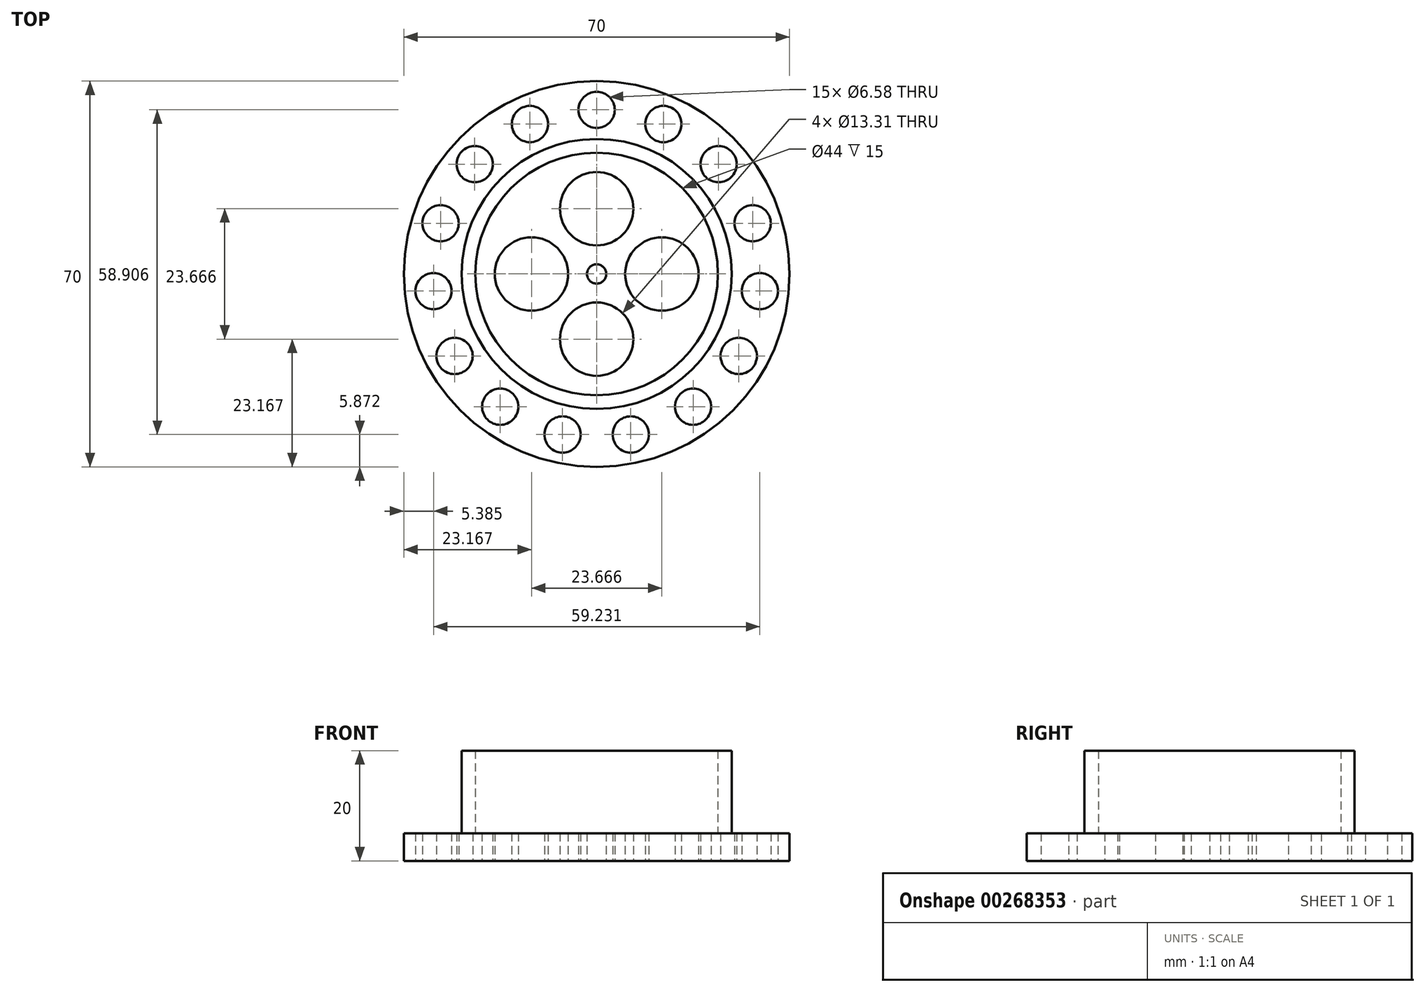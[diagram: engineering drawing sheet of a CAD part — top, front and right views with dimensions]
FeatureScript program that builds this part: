
annotation { "Feature Type Name" : "Feature", "Feature Type Description" : "" }
export const myFeature = defineFeature(function(context is Context, id is Id, definition is map)
    precondition{}
    {
        {
            var Q0;
            Q0=qCreatedBy(makeId("Top.planeOp"),FACE);
            var sketch = newSketch(context, id + "F0", { "sketchPlane" : qUnion([Q0])});
            skCircle(sketch, "E0", {"center": v(0, 0) * mm, "radius": 35 * mm});
            skCircle(sketch, "E1", {"center": v(0, 0) * mm, "radius": 22 * mm});
            skCircle(sketch, "E2", {"center": v(0, 0) * mm, "radius": 24.5 * mm});
            skCircle(sketch, "E3", {"center": v(0, 0) * mm, "radius": 1.75 * mm});
            skCircle(sketch, "E4", {"center": v(0, 11.83) * mm, "radius": 6.66 * mm});
            skCircle(sketch, "E5", {"center": v(0, 29.78) * mm, "radius": 3.29 * mm});
            skCircle(sketch, "E6.1.0", {"center": v(-12.11, 27.2) * mm, "radius": 3.29 * mm});
            skCircle(sketch, "E6.2.0", {"center": v(-22.13, 19.93) * mm, "radius": 3.29 * mm});
            skCircle(sketch, "E6.3.0", {"center": v(-28.32, 9.2) * mm, "radius": 3.29 * mm});
            skCircle(sketch, "E6.4.0", {"center": v(-29.62, -3.11) * mm, "radius": 3.29 * mm});
            skCircle(sketch, "E6.5.0", {"center": v(-25.79, -14.89) * mm, "radius": 3.29 * mm});
            skCircle(sketch, "E6.6.0", {"center": v(-17.5, -24.1) * mm, "radius": 3.29 * mm});
            skCircle(sketch, "E6.7.0", {"center": v(-6.2, -29.13) * mm, "radius": 3.29 * mm});
            skCircle(sketch, "E6.8.0", {"center": v(6.2, -29.13) * mm, "radius": 3.29 * mm});
            skCircle(sketch, "E6.9.0", {"center": v(17.5, -24.1) * mm, "radius": 3.29 * mm});
            skCircle(sketch, "E6.10.0", {"center": v(25.79, -14.89) * mm, "radius": 3.29 * mm});
            skCircle(sketch, "E6.11.0", {"center": v(29.62, -3.11) * mm, "radius": 3.29 * mm});
            skCircle(sketch, "E6.12.0", {"center": v(28.32, 9.2) * mm, "radius": 3.29 * mm});
            skCircle(sketch, "E6.13.0", {"center": v(22.13, 19.93) * mm, "radius": 3.29 * mm});
            skCircle(sketch, "E6.14.0", {"center": v(12.11, 27.2) * mm, "radius": 3.29 * mm});
            skCircle(sketch, "E7.1.0", {"center": v(-11.83, 0) * mm, "radius": 6.66 * mm});
            skCircle(sketch, "E7.2.0", {"center": v(0, -11.83) * mm, "radius": 6.66 * mm});
            skCircle(sketch, "E7.3.0", {"center": v(11.83, 0) * mm, "radius": 6.66 * mm});
            skSolve(sketch);
        }
        {
            var Q0;
            Q0=qSketchRegion(id+"F0",true);
            var Q1;
            Q1=makeQuery(id+"F0.imprint","IMPRINT",FACE,{"disambiguationData":[TD([[makeQuery(id+"F0.imprint","IMPRINT",EDGE,{"derivedFrom":sQuery(id+"F0.wireOp",EDGE,"E1")}),1.0]])]});
            var Q2;
            Q2=makeQuery(id+"F0.imprint","IMPRINT",FACE,{"disambiguationData":[TD([[makeQuery(id+"F0.imprint","IMPRINT",EDGE,{"derivedFrom":sQuery(id+"F0.wireOp",EDGE,"E1")}),-1.0]])]});
            extrude(context, id + "F1", {"entities" : qUnion([Q0, Q1, Q2]), "depth" : 5 * mm});
        }
        {
            var Q0;
            Q0=makeQuery(id+"F0.imprint","IMPRINT",FACE,{"disambiguationData":[TD([[makeQuery(id+"F0.imprint","IMPRINT",EDGE,{"derivedFrom":sQuery(id+"F0.wireOp",EDGE,"E1")}),-1.0]])]});
            extrude(context, id + "F2", {"entities" : qUnion([Q0]), "operationType" : NewBodyOperationType.ADD, "depth" : 20 * mm});
        }
        {
            var Q0;
            Q0=makeQuery(id+"F0.imprint","IMPRINT",FACE,{"disambiguationData":[TD([[makeQuery(id+"F0.imprint","IMPRINT",EDGE,{"derivedFrom":sQuery(id+"F0.wireOp",EDGE,"E0")}),1.0]])]});
            extrude(context, id + "F3", {"entities" : qUnion([Q0]), "operationType" : NewBodyOperationType.ADD, "depth" : 3 * mm});
        }
    });
